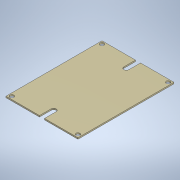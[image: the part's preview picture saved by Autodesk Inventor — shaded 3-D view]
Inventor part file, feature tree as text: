
AUTODESK INVENTOR PART (.ipt)
format: ipt  version: 2022 (Build 260153000, 153)  size: 175,616 bytes
history: native  units: in
note: dims shown in document units (in); Inventor stores cm internally (conversion verified against a paired STEP export)
features: sketch x3, extrude x2, hole x1
ambient origin geometry x8: Origin, YZ Plane, XZ Plane, XY Plane, X Axis, Y Axis, Z Axis, Center Point
bodies: Body1 (feature_tree)
feature tree (6):
  extrude  "Extrusion2"  Depth=2.2638in
  extrude  "Extrusion3"  Depth=0.1181in
  hole  "Hole1"  [1 undecoded]
  sketch  "Sketch2"  dims[d28=1.6969in d29=2.2638in]
  sketch  "Sketch3"  dims[d30=0.0315in d31=0.0in d32=0.1181in]
  sketch  "Sketch4"  dims[d33=0.2756in d34=0.0591in d35=0.0in d36=0.0in d37=0.0689in d38=0.0689in d39=0.0689in d40=0.0689in d41=0.0945in d42=0.1575in d43=0.1732in d44=0.0787in d45=0.6181in d46=0.315in d47=0.8108in]
note: 1 required parameter value undecoded (feature->parameter linkage not recoverable at this tier; creation-order binding heuristic only, values carry confidence <= 0.55)
